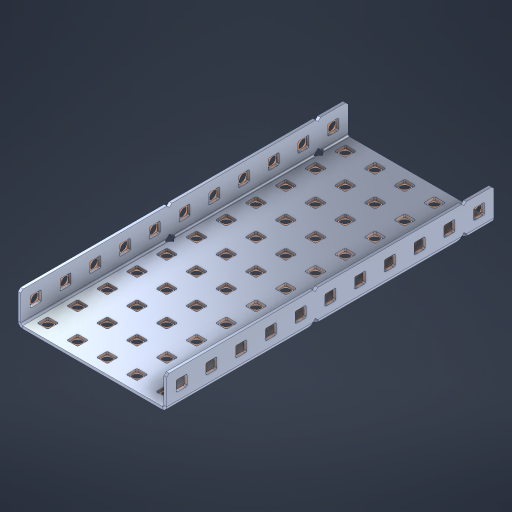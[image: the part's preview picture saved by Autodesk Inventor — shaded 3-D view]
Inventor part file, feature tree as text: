
AUTODESK INVENTOR PART (.ipt)
format: ipt  version: 2023 (Build 270158000, 158)  size: 1,107,968 bytes
history: native  units: in
note: dims shown in document units (in); Inventor stores cm internally (conversion verified against a paired STEP export)
features: other x82, extrude x76, sheet_metal_op x10, sketch x8, mirror x1, pattern_linear x1, chamfer x1
ambient origin geometry x8: Origin, YZ Plane, XZ Plane, XY Plane, X Axis, Y Axis, Z Axis, Center Point
bodies: Solid1 (feature_tree), Body (feature_tree)
feature tree (179):
  other  "Flange Pattern Plane"
  sheet_metal_op  "Flange Pattern"
  sheet_metal_op  "Body Pattern"
  other  "Arc Length"
  mirror  "Notch Mirror"
  pattern_linear  "Notch Pattern"  Spacing1=0.1875in  [1 undecoded]
  chamfer  "End Chamfer"
  extrude  "Half Cut"  Depth=0.0469in
  sketch  "Sketch1"  dims[d0=2.5in]
  other  "Plate1"
  sketch  "Sketch2"  dims[d1=5.5in]
  other  "Plate2"
  sheet_metal_op  "Bend1"
  sheet_metal_op  "Corner1"
  sketch  "Sketch3"  dims[d2=0.0469in]
  other  "Flange Pattern Sketch"
  sketch  "Sketch7"  dims[d3=0.0469in]
  other  "Srf1"
  other  "Srf2"
  sketch  "Sketch8"  dims[d4=0.0234in]
  sketch  "Sketch9"  dims[d5=0.0938in]
  other  "Srf91"
  sheet_metal_op  "Body Pattern Sketch"
  other  "Srf92"
  sketch  "Sketch13"  dims[d6=0.0469in]
  sketch  "Sketch14"  dims[d7=0.5in d8=90.0deg d9=0.0312in d10=0.1875in d11=0.0469in d12=0.0469in d16=0.182in d17=0.02in d18=0.0469in d19=0.0in d20=0.25in d21=0.25in d46=0.172in d47=1.0in d48=0.0in d49=0.182in d50=0.02in d51=0.25in d52=0.25in d53=0.0469in d54=0.0in d55=0.172in d56=1.0in d57=0.0in d60=4.3307in d62=0.5in d63=1.9685in d65=0.5in d85=0.1227in d86=0.1659in d88=0.04in d89=0.0469in d90=0.0in d91=0.04in d92=0.0491in d95=2.5in d96=0.04in d97=0.25in d98=45.0deg d101=0.0in d102=2.497in d131=2.5in d132=4.3307in d134=0.5in d139=0.5in]
  other  "Srf856"
  other  "Srf1310"
  other  "Srf1311"
  other  "Srf1312"
  other  "Srf1376"
  other  "Srf1377"
  other  "Srf1728"
  other  "Srf1755"
  other  "Srf1878"
  other  "Srf1879"
  other  "Srf1880"
  other  "Srf1881"
  other  "Srf1882"
  other  "Srf1883"
  other  "Srf1884"
  other  "Srf1885"
  other  "Srf1886"
  other  "Srf1887"
  other  "Srf1888"
  other  "Srf1889"
  other  "Srf1890"
  other  "Srf1891"
  other  "Srf1892"
  other  "Srf1893"
  other  "Srf1942"
  other  "Srf1943"
  other  "Srf1944"
  other  "Srf1945"
  other  "Srf1946"
  other  "Srf1947"
  other  "Srf1948"
  other  "Srf1949"
  other  "Srf1950"
  other  "Srf1951"
  other  "Srf1952"
  other  "Srf1953"
  other  "Srf1954"
  other  "Srf1955"
  other  "Srf1956"
  other  "Srf1957"
  other  "Srf1958"
  other  "Srf1959"
  other  "Srf1960"
  other  "Srf1961"
  other  "Srf1962"
  other  "Srf1963"
  other  "Srf1964"
  other  "Srf1965"
  other  "Srf1966"
  other  "Srf1967"
  other  "Srf1968"
  other  "Srf1969"
  other  "Srf1970"
  other  "Srf2146"
  other  "Srf2147"
  other  "Srf2148"
  other  "Srf2149"
  other  "Srf2150"
  other  "Srf2151"
  other  "Srf2152"
  other  "Srf2153"
  other  "Srf2154"
  other  "Srf2155"
  other  "Srf2156"
  other  "Srf2157"
  other  "Srf2158"
  other  "Srf2159"
  other  "Srf2160"
  other  "Srf2161"
  other  "Srf2162"
  other  "Srf2163"
  other  "Srf2164"
  other  "Srf2165"
  sheet_metal_op  "Flange Stamp"
  sheet_metal_op  "Flange Circle"
  sheet_metal_op  "Body Stamp"
  sheet_metal_op  "Body Circle"
  sheet_metal_op  "Notch"
  extrude  "ExtrusionSrf2"  Depth=0.0469in
  extrude  "ExtrusionSrf92"  Depth=2.5in
  extrude  "ExtrusionSrf856"  Depth=0.02in
  extrude  "ExtrusionSrf1310"  Depth=0.0469in
  extrude  "ExtrusionSrf1311"  TaperAngle=0.0deg  [1 undecoded]
  extrude  "ExtrusionSrf1312"  Depth=0.25in
  extrude  "ExtrusionSrf1376"  Depth=0.25in
  extrude  "ExtrusionSrf1377"  Depth=2.5in
  extrude  "ExtrusionSrf1728"  Depth=2.5in TaperAngle=0.0deg
  extrude  "ExtrusionSrf1755"  Depth=2.5in
  extrude  "ExtrusionSrf1878"  Depth=0.02in
  extrude  "ExtrusionSrf1879"  Depth=0.25in
  extrude  "ExtrusionSrf1880"  Depth=0.25in
  extrude  "ExtrusionSrf1881"  Depth=0.0469in
  extrude  "ExtrusionSrf1882"  TaperAngle=0.0deg  [1 undecoded]
  extrude  "ExtrusionSrf1883"  Depth=2.5in
  extrude  "ExtrusionSrf1884"  Depth=2.5in TaperAngle=0.0deg
  extrude  "ExtrusionSrf1885"  Depth=2.5in
  extrude  "ExtrusionSrf1886"  Depth=2.5in
  extrude  "ExtrusionSrf1887"  Depth=2.5in
  extrude  "ExtrusionSrf1888"  Depth=2.5in
  extrude  "ExtrusionSrf1889"  Depth=2.5in
  extrude  "ExtrusionSrf1890"  Depth=0.0469in
  extrude  "ExtrusionSrf1891"  TaperAngle=0.0deg  [1 undecoded]
  extrude  "ExtrusionSrf1892"  Depth=2.5in
  extrude  "ExtrusionSrf1893"  Depth=2.5in
  extrude  "ExtrusionSrf1942"  Depth=2.5in
  extrude  "ExtrusionSrf1943"  Depth=0.25in TaperAngle=45.0deg
  extrude  "ExtrusionSrf1944"  TaperAngle=0.0deg  [1 undecoded]
  extrude  "ExtrusionSrf1945"  Depth=2.5in
  extrude  "ExtrusionSrf1946"  Depth=2.5in
  extrude  "ExtrusionSrf1947"  Depth=2.5in
  extrude  "ExtrusionSrf1948"  Depth=2.5in
  extrude  "ExtrusionSrf1949"  Depth=2.5in
  extrude  "ExtrusionSrf1950"  [1 undecoded]
  extrude  "ExtrusionSrf1951"  [1 undecoded]
  extrude  "ExtrusionSrf1952"  [1 undecoded]
  extrude  "ExtrusionSrf1953"  [1 undecoded]
  extrude  "ExtrusionSrf1954"  [1 undecoded]
  extrude  "ExtrusionSrf1955"  [1 undecoded]
  extrude  "ExtrusionSrf1956"  [1 undecoded]
  extrude  "ExtrusionSrf1957"  [1 undecoded]
  extrude  "ExtrusionSrf1958"  [1 undecoded]
  extrude  "ExtrusionSrf1959"  [1 undecoded]
  extrude  "ExtrusionSrf1960"  [1 undecoded]
  extrude  "ExtrusionSrf1961"  [1 undecoded]
  extrude  "ExtrusionSrf1962"  [1 undecoded]
  extrude  "ExtrusionSrf1963"  [1 undecoded]
  extrude  "ExtrusionSrf1964"  [1 undecoded]
  extrude  "ExtrusionSrf1965"  [1 undecoded]
  extrude  "ExtrusionSrf1966"  [1 undecoded]
  extrude  "ExtrusionSrf1967"  [1 undecoded]
  extrude  "ExtrusionSrf1968"  [1 undecoded]
  extrude  "ExtrusionSrf1969"  [1 undecoded]
  extrude  "ExtrusionSrf1970"  [1 undecoded]
  extrude  "ExtrusionSrf2146"  [1 undecoded]
  extrude  "ExtrusionSrf2147"  [1 undecoded]
  extrude  "ExtrusionSrf2148"  [1 undecoded]
  extrude  "ExtrusionSrf2149"  [1 undecoded]
  extrude  "ExtrusionSrf2150"  [1 undecoded]
  extrude  "ExtrusionSrf2151"  [1 undecoded]
  extrude  "ExtrusionSrf2152"  [1 undecoded]
  extrude  "ExtrusionSrf2153"  [1 undecoded]
  extrude  "ExtrusionSrf2154"  [1 undecoded]
  extrude  "ExtrusionSrf2155"  [1 undecoded]
  extrude  "ExtrusionSrf2156"  [1 undecoded]
  extrude  "ExtrusionSrf2157"  [1 undecoded]
  extrude  "ExtrusionSrf2158"  [1 undecoded]
  extrude  "ExtrusionSrf2159"  [1 undecoded]
  extrude  "ExtrusionSrf2160"  [1 undecoded]
  extrude  "ExtrusionSrf2161"  [1 undecoded]
  extrude  "ExtrusionSrf2162"  [1 undecoded]
  extrude  "ExtrusionSrf2163"  [1 undecoded]
  extrude  "ExtrusionSrf2164"  [1 undecoded]
  extrude  "ExtrusionSrf2165"  [1 undecoded]
note: 46 required parameter values undecoded (feature->parameter linkage not recoverable at this tier; creation-order binding heuristic only, values carry confidence <= 0.55)
